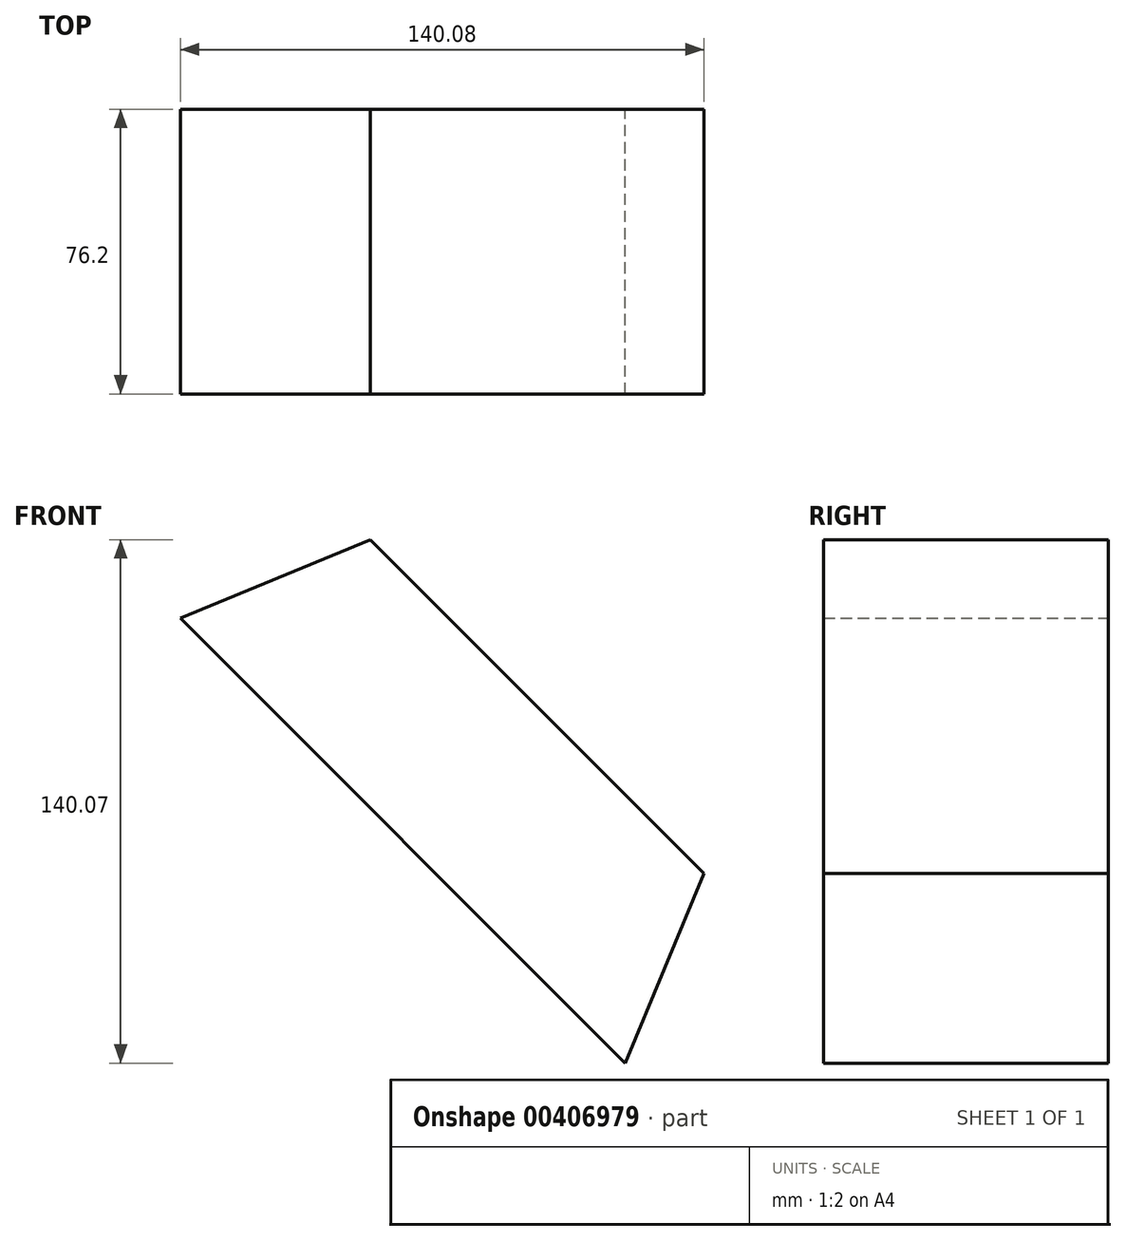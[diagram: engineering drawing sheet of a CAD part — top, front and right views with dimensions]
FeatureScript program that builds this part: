
annotation { "Feature Type Name" : "Feature", "Feature Type Description" : "" }
export const myFeature = defineFeature(function(context is Context, id is Id, definition is map)
    precondition{}
    {
        {
            var Q0;
            Q0=qCreatedBy(makeId("Front.planeOp"),FACE);
            var sketch = newSketch(context, id + "F0", { "sketchPlane" : qUnion([Q0])});
            skLineSegment(sketch, "E0", {"start": v(-57.32, 154.32) * mm, "end": v(68.93, 154.32) * mm, "construction": true});
            skLineSegment(sketch, "E1", {"start": v(68.93, 154.32) * mm, "end": v(158.2, 65.04) * mm, "construction": true});
            skLineSegment(sketch, "E2", {"start": v(158.2, 65.04) * mm, "end": v(158.2, -61.2) * mm, "construction": true});
            skLineSegment(sketch, "E3", {"start": v(158.2, -61.2) * mm, "end": v(68.93, -150.48) * mm, "construction": true});
            skLineSegment(sketch, "E4", {"start": v(68.93, -150.48) * mm, "end": v(-57.32, -150.48) * mm, "construction": true});
            skLineSegment(sketch, "E5", {"start": v(-57.32, -150.48) * mm, "end": v(-146.6, -61.2) * mm});
            skLineSegment(sketch, "E6", {"start": v(-146.6, -61.2) * mm, "end": v(-146.6, 65.04) * mm, "construction": true});
            skLineSegment(sketch, "E7", {"start": v(-146.6, 65.04) * mm, "end": v(-57.32, 154.32) * mm, "construction": true});
            skLineSegment(sketch, "E8", {"start": v(-78.36, 205.12) * mm, "end": v(89.97, 205.12) * mm, "construction": true});
            skLineSegment(sketch, "E9", {"start": v(89.97, 205.12) * mm, "end": v(209, 86.08) * mm, "construction": true});
            skLineSegment(sketch, "E10", {"start": v(209, 86.08) * mm, "end": v(209, -82.25) * mm, "construction": true});
            skLineSegment(sketch, "E11", {"start": v(209, -82.25) * mm, "end": v(89.97, -201.28) * mm, "construction": true});
            skLineSegment(sketch, "E12", {"start": v(89.97, -201.28) * mm, "end": v(-78.36, -201.28) * mm, "construction": true});
            skLineSegment(sketch, "E13", {"start": v(-78.36, -201.28) * mm, "end": v(-197.4, -82.25) * mm});
            skLineSegment(sketch, "E14", {"start": v(-197.4, -82.25) * mm, "end": v(-197.4, 86.08) * mm, "construction": true});
            skLineSegment(sketch, "E15", {"start": v(-197.4, 86.08) * mm, "end": v(-78.36, 205.12) * mm, "construction": true});
            skLineSegment(sketch, "E16", {"start": v(-197.4, 1.92) * mm, "end": v(209, 1.92) * mm, "construction": true});
            skPoint(sketch, "E17", {"position": v(5.8, 1.92) * mm});
            skLineSegment(sketch, "E18", {"start": v(5.8, 154.32) * mm, "end": v(5.8, -150.48) * mm, "construction": true});
            skLineSegment(sketch, "E19", {"start": v(-78.36, 205.12) * mm, "end": v(-57.32, 154.32) * mm, "construction": true});
            skLineSegment(sketch, "E20", {"start": v(68.93, 154.32) * mm, "end": v(89.97, 205.12) * mm, "construction": true});
            skLineSegment(sketch, "E21", {"start": v(209, 86.08) * mm, "end": v(158.2, 65.04) * mm, "construction": true});
            skLineSegment(sketch, "E22", {"start": v(209, -82.25) * mm, "end": v(158.2, -61.2) * mm, "construction": true});
            skLineSegment(sketch, "E23", {"start": v(68.93, -150.48) * mm, "end": v(89.97, -201.28) * mm, "construction": true});
            skLineSegment(sketch, "E24", {"start": v(-57.32, -150.48) * mm, "end": v(-78.36, -201.28) * mm});
            skLineSegment(sketch, "E25", {"start": v(-146.6, -61.2) * mm, "end": v(-197.4, -82.25) * mm});
            skLineSegment(sketch, "E26", {"start": v(-146.6, 65.04) * mm, "end": v(-197.4, 86.08) * mm, "construction": true});
            skSolve(sketch);
        }
        {
            var Q0;
            Q0=makeQuery(id+"F0.imprint","IMPRINT",FACE,{"disambiguationData":[TD([[makeQuery(id+"F0.imprint","IMPRINT",EDGE,{"derivedFrom":sQuery(id+"F0.wireOp",EDGE,"E5")}),1.0]])]});
            extrude(context, id + "F1", {"entities" : qUnion([Q0]), "depth" : 76.2 * mm});
        }
    });
